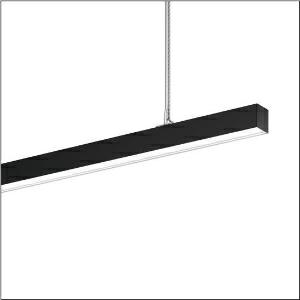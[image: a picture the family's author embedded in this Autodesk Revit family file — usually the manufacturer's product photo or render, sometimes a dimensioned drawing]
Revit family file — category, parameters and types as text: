
# Revit family: silica_r__21_51mx33tbt9b_b685
name_source: partatom
category: Lighting Fixtures
units: mm (PartAtom-declared; Revit-internal decimal feet)

## family parameters
Cut with Voids When Loaded = No
Host = Face
Light Source = No
Part Type = Normal
Room Calculation Point = No
Round Connector Dimension = Use Diameter
Shared = No

## types (1)
- --- (1 x LED, 7170 lm, 67.4 W, 6500K)
    Apparent Load = 67 VA
    CIE Flux Codes = 78 96 99 56 100
    Color Rendering = 80
    Color Temperature = 6500K
    Default Elevation = 1800 mm
    Description = Silica® 21, office luminaire, primary optical cover: prismatic diffuser, of PMMA, CAT 2 (L<= 3000cd/m²), light emission: direct/indirect distribution, primary light characteristic: symmetric, installation type: suspended mounting, LED, rated luminous flux: 7.170lm, luminous efficacy: 101lm/W, light colour: 8tw, colour temperature: 2700..6500K, control gear: ECG DALI, with terminal, 3+2-pole, max. 2.5mm², mains connection: 220..240V, AC, 50/60Hz, rated input power: 70.8W, luminaire housing, of aluminium, jet black (RAL 9005), length: 1.504mm, width: 53mm, height: 53mm, protection rating (complete): IP20, insulation class (complete): insulation class I (protective earthing), certification: CE, permissible operating ambient temperature: 0..+35°C, standard: EN 50419, packaging unit: 1 piece
    Height = 53 mm
    Lamp = 1 x LED
    Lamp Light Flux = 7170 lm
    Lamp Power = 67.4 W
    Lamp count = 1
    Length = 1504 mm
    Luminous efficacy = 106 lm/W
    Manufacturer = Siteco
    ModVariant = No
    Model = 51MX33TBT9B
    Mounting Place = Ceiling
    Mounting Type = Pendant
    Number of Poles = 1
    OnlyDefault = Yes
    Power Factor = 1
    Product Name = Silica® 21
    Product group = office luminaire | ceiling pendant
    ProductGroupID = 902
    Protection Class = Protection class I
    Protection Degree = IP 20
    RLX_Detail_Level = 1
    RLX_Emergency_Light_Flux = 0 lm
    RLX_Emergency_Type = 0
    RLX_Emergency_Type_DB = No
    RlxData = <blob elided: 22937 chars, md5=d8d96f4d>
    Socket = socket
    Standby Power = 0 W
    System Light Flux = 7170 lm
    System Power = 67 W
    Type Comments = individual setting
    Type Image = l_1313646.jpg
    URL = http://relux.com
    VarID = @adj_089127
    Voltage = 0 V
    Weight = 0.00 kg
    Width = 53 mm

## geometry (parser evidence)
native form markers: Blend x4, Sweep x12
no freeform markers — native parametric forms only
